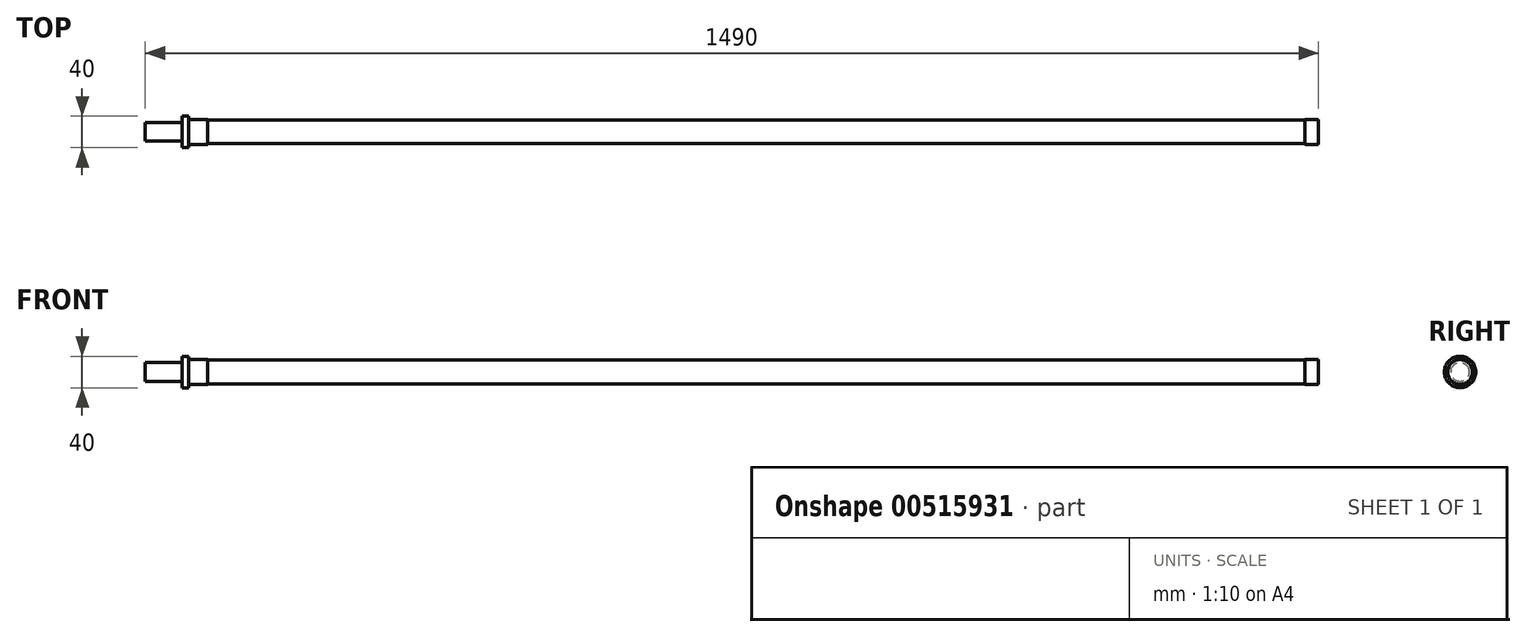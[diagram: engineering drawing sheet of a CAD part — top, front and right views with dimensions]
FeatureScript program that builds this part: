
annotation { "Feature Type Name" : "Feature", "Feature Type Description" : "" }
export const myFeature = defineFeature(function(context is Context, id is Id, definition is map)
    precondition{}
    {
        {
            var Q0;
            Q0=qCreatedBy(makeId("Top.planeOp"),FACE);
            var sketch = newSketch(context, id + "F0", { "sketchPlane" : qUnion([Q0])});
            skLineSegment(sketch, "E0", {"start": v(0, 0) * mm, "end": v(0, 11.9) * mm});
            skLineSegment(sketch, "E1", {"start": v(0, 11.9) * mm, "end": v(47, 11.9) * mm});
            skLineSegment(sketch, "E2", {"start": v(47, 11.9) * mm, "end": v(47, 20) * mm});
            skLineSegment(sketch, "E3", {"start": v(47, 20) * mm, "end": v(55, 20) * mm});
            skLineSegment(sketch, "E4", {"start": v(55, 20) * mm, "end": v(55, 15.75) * mm});
            skLineSegment(sketch, "E5", {"start": v(55, 15.75) * mm, "end": v(79, 15.75) * mm});
            skLineSegment(sketch, "E6", {"start": v(79, 15.75) * mm, "end": v(79, 15) * mm});
            skLineSegment(sketch, "E7", {"start": v(79, 15) * mm, "end": v(1473, 15) * mm});
            skLineSegment(sketch, "E8", {"start": v(1473, 15) * mm, "end": v(1473, 15.75) * mm});
            skLineSegment(sketch, "E9", {"start": v(1473, 15.75) * mm, "end": v(1490, 15.75) * mm});
            skLineSegment(sketch, "E10", {"start": v(1490, 15.75) * mm, "end": v(1490, 0) * mm});
            skLineSegment(sketch, "E11", {"start": v(1490, 0) * mm, "end": v(0, 0) * mm});
            skLineSegment(sketch, "E12", {"start": v(835.15, 0) * mm, "end": v(1490, 0) * mm, "construction": true});
            skSolve(sketch);
        }
        {
            var Q0;
            Q0=makeQuery(id+"F0.imprint","IMPRINT",FACE,{"disambiguationData":[TD([[makeQuery(id+"F0.imprint","IMPRINT",EDGE,{"derivedFrom":sQuery(id+"F0.wireOp",EDGE,"E0")}),-1.0]])]});
            var Q1;
            Q1=sQuery(id+"F0.wireOp",EDGE,"E12");
            revolve(context, id + "F1", {"entities" : qUnion([Q0]), "axis" : qUnion([Q1]), "revolveType" : RevolveType.FULL});
        }
    });
